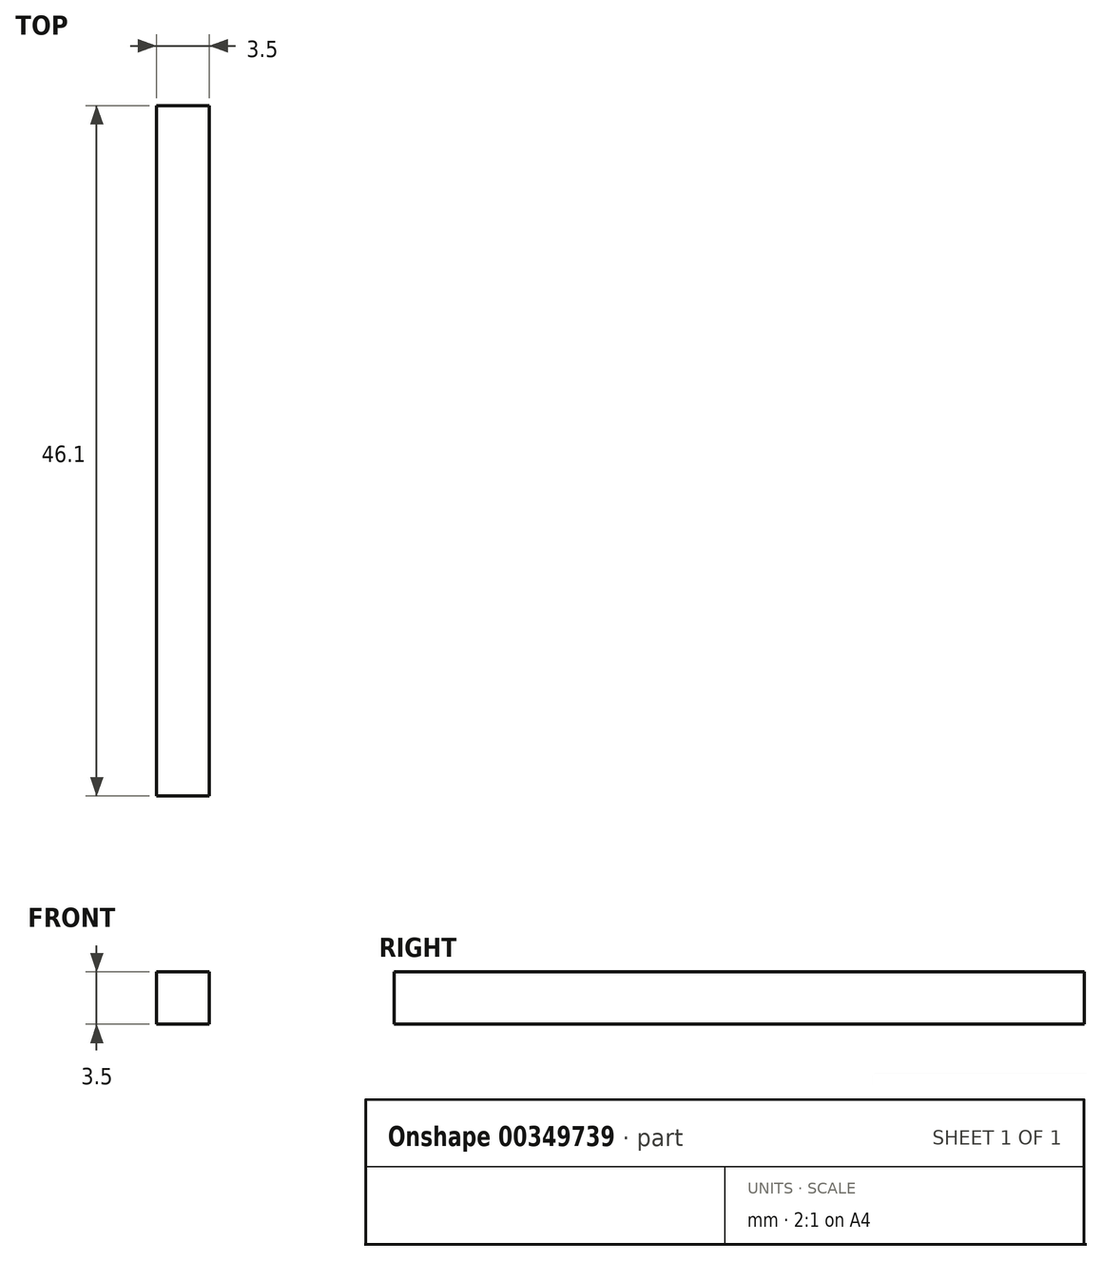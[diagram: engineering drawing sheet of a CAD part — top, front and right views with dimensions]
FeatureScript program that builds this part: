
annotation { "Feature Type Name" : "Feature", "Feature Type Description" : "" }
export const myFeature = defineFeature(function(context is Context, id is Id, definition is map)
    precondition{}
    {
        {
            var Q0;
            Q0=qCreatedBy(makeId("Top.planeOp"),FACE);
            var sketch = newSketch(context, id + "F0", { "sketchPlane" : qUnion([Q0])});
            skLineSegment(sketch, "E0.bottom", {"start": v(1.75, -23.05) * mm, "end": v(-1.75, -23.05) * mm});
            skLineSegment(sketch, "E0.top", {"start": v(1.75, 23.05) * mm, "end": v(-1.75, 23.05) * mm});
            skLineSegment(sketch, "E0.left", {"start": v(1.75, -23.05) * mm, "end": v(1.75, 23.05) * mm});
            skLineSegment(sketch, "E0.right", {"start": v(-1.75, -23.05) * mm, "end": v(-1.75, 23.05) * mm});
            skPoint(sketch, "E0.middle", {"position": v(0, 0) * mm});
            skSolve(sketch);
        }
        {
            var Q0;
            Q0=qSketchRegion(id+"F0",true);
            extrude(context, id + "F1", {"entities" : qUnion([Q0]), "depth" : 3.5 * mm});
        }
    });
